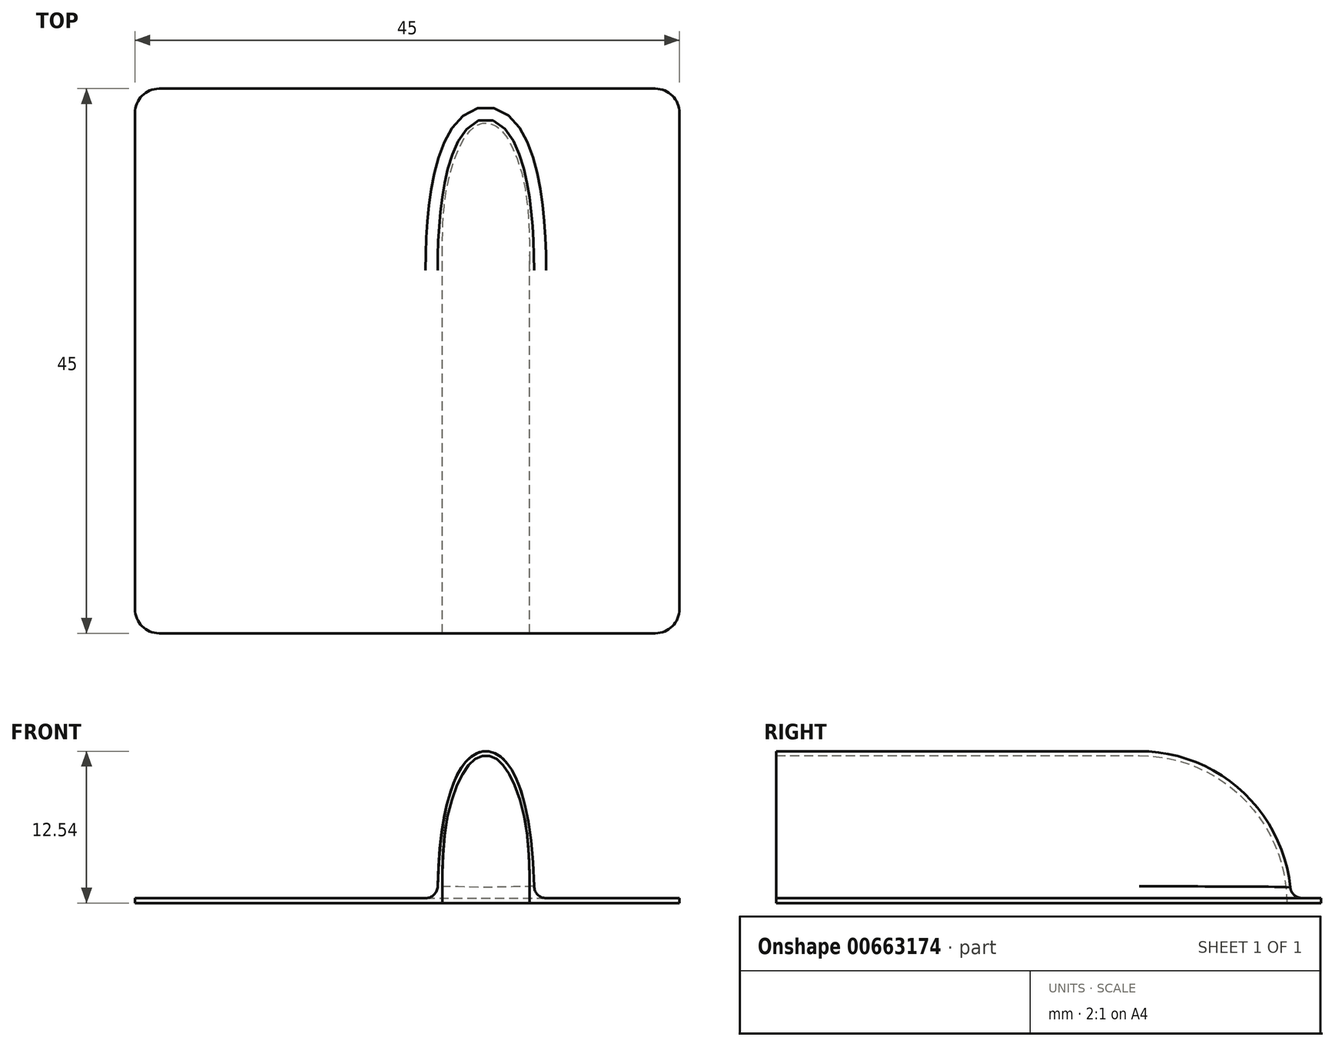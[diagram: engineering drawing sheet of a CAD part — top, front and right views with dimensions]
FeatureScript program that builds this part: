
annotation { "Feature Type Name" : "Feature", "Feature Type Description" : "" }
export const myFeature = defineFeature(function(context is Context, id is Id, definition is map)
    precondition{}
    {
        {
            var Q0;
            Q0=qCreatedBy(makeId("Top.planeOp"),FACE);
            var sketch = newSketch(context, id + "F0", { "sketchPlane" : qUnion([Q0])});
            skLineSegment(sketch, "E0.bottom", {"start": v(2, 45) * mm, "end": v(43, 45) * mm});
            skLineSegment(sketch, "E0.top", {"start": v(2, 0) * mm, "end": v(25, 0) * mm});
            skLineSegment(sketch, "E0.left", {"start": v(0, 43) * mm, "end": v(0, 2) * mm});
            skLineSegment(sketch, "E0.right", {"start": v(45, 43) * mm, "end": v(45, 2) * mm});
            skLineSegment(sketch, "E1.trimOffspring", {"start": v(33, 0) * mm, "end": v(43, 0) * mm});
            skLineSegment(sketch, "E2", {"start": v(25, 0) * mm, "end": v(25, 30) * mm});
            skLineSegment(sketch, "E3", {"start": v(33, 30) * mm, "end": v(33, 0) * mm});
            skPoint(sketch, "E4.visualSharp", {"position": v(0, 45) * mm});
            skArc(sketch, "E4.filletArc", {"start": v(2, 45) * mm, "mid": v(0.59, 44.41) * mm, "end": v(0, 43) * mm});
            skPoint(sketch, "E5.visualSharp", {"position": v(45, 45) * mm});
            skArc(sketch, "E5.filletArc", {"start": v(45, 43) * mm, "mid": v(44.41, 44.41) * mm, "end": v(43, 45) * mm});
            skPoint(sketch, "E6.visualSharp", {"position": v(45, 0) * mm});
            skArc(sketch, "E6.filletArc", {"start": v(43, 0) * mm, "mid": v(44.41, 0.59) * mm, "end": v(45, 2) * mm});
            skPoint(sketch, "E7.visualSharp", {"position": v(0, 0) * mm});
            skArc(sketch, "E7.filletArc", {"start": v(0, 2) * mm, "mid": v(0.59, 0.59) * mm, "end": v(2, 0) * mm});
            skFitSpline(sketch, "E8", {"points": [v(25, 30) * mm, v(29, 42.54) * mm, v(33, 30) * mm], "startDerivative": vector(0, 54.87) * mm, "endDerivative": vector(0, -54.87) * mm});
            skSolve(sketch);
        }
        {
            var Q0;
            Q0=qCreatedBy(makeId("Top.planeOp"),FACE);
            var sketch = newSketch(context, id + "F1", { "sketchPlane" : qUnion([Q0])});
            skFitSpline(sketch, "E9", {"points": [v(25, 30) * mm, v(29, 42.54) * mm, v(33, 30) * mm], "startDerivative": vector(0, 54.87) * mm, "endDerivative": vector(0, -54.87) * mm});
            skFitSpline(sketch, "E10.0", {"points": [v(25.4, 30) * mm, v(25.4, 32.27) * mm, v(25.65, 36.1) * mm, v(26.42, 39.23) * mm, v(27.2, 40.85) * mm, v(27.81, 41.64) * mm, v(28.42, 42.06) * mm, v(29, 42.18) * mm, v(29.58, 42.06) * mm, v(30.19, 41.64) * mm, v(30.8, 40.85) * mm, v(31.58, 39.23) * mm, v(32.35, 36.1) * mm, v(32.6, 32.27) * mm, v(32.6, 30) * mm]});
            skLineSegment(sketch, "E11", {"start": v(25, 30) * mm, "end": v(25.4, 30) * mm});
            skLineSegment(sketch, "E12", {"start": v(32.6, 30) * mm, "end": v(33, 30) * mm});
            skSolve(sketch);
        }
        {
            var Q0;
            Q0=qCreatedBy(makeId("Top.planeOp"),FACE);
            var sketch = newSketch(context, id + "F2", { "sketchPlane" : qUnion([Q0])});
            skLineSegment(sketch, "E13", {"start": v(20, 30) * mm, "end": v(28, 30) * mm});
            skSolve(sketch);
        }
        {
            var Q0;
            Q0=makeQuery(id+"F0.imprint","IMPRINT",FACE,{"disambiguationData":[TD([[makeQuery(id+"F0.imprint","IMPRINT",EDGE,{"derivedFrom":sQuery(id+"F0.wireOp",EDGE,"E0.bottom")}),-1.0]])]});
            extrude(context, id + "F3", {"entities" : qUnion([Q0]), "depth" : .4 * mm, "offsetDistance" : 25 * mm});
        }
        {
            var Q0;
            Q0=makeQuery(id+"F1.imprint","IMPRINT",FACE,{"disambiguationData":[TD([[makeQuery(id+"F1.imprint","IMPRINT",EDGE,{"derivedFrom":sQuery(id+"F1.wireOp",EDGE,"E9")}),-1.0]])]});
            var Q1;
            Q1=sQuery(id+"F2.wireOp",EDGE,"E13");
            revolve(context, id + "F4", {"operationType" : NewBodyOperationType.ADD, "entities" : qUnion([Q0]), "axis" : qUnion([Q1]), "revolveType" : RevolveType.ONE_DIRECTION, "angle" : 90 * degree});
        }
        {
            var Q0;
            Q0=makeQuery(id+"F4.opRevolve","CAP_FACE",FACE,{"disambiguationData":[OSD([sQuery(id+"F1.wireOp",EDGE,"E9"),sQuery(id+"F1.wireOp",EDGE,"E10.0"),sQuery(id+"F1.wireOp",EDGE,"E11"),sQuery(id+"F1.wireOp",EDGE,"E12")])],"isStart":false});
            var Q1;
            Q1 = qSketchRegion(id + "F2", true);
            extrude(context, id + "F5", {"entities" : qUnion([Q0, Q1]), "operationType" : NewBodyOperationType.ADD, "depth" : 30 * mm, "offsetDistance" : 25 * mm});
        }
        {
            var Q0;
            {var subQ0=sQuery(id+"F0.wireOp",EDGE,"E3");Q0=makeQuery(id+"F5.boolean.opBoolean","MERGE",EDGE,{"derivedFrom":[makeQuery(id+"F3.opExtrude","CAP_EDGE",EDGE,{"disambiguationData":[OSD([subQ0])],"isStart":false}),makeQuery(id+"F5.opExtrude","SWEPT_EDGE",EDGE,{"disambiguationData":[OSD([subQ0,sQuery(id+"F0.wireOp",EDGE,"E8")])]})]});}
            var Q1;
            {var subQ0=sQuery(id+"F1.wireOp",EDGE,"E9");Q1=makeQuery(id+"F5.boolean.opBoolean","MERGE",EDGE,{"derivedFrom":[makeQuery(id+"F4.boolean.opBoolean","SPLIT",EDGE,{"derivedFrom":makeQuery(id+"F4.opRevolve","CAP_EDGE",EDGE,{"disambiguationData":[OSD([subQ0])],"isStart":false})}),makeQuery(id+"F5.opExtrude","CAP_EDGE",EDGE,{"disambiguationData":[OSD([subQ0])],"isStart":true})]});}
            fillet(context, id + "F6", {"entities" : qUnion([Q0, Q1]), "radius" : 1 * mm, "tangentPropagation" : true, "allowEdgeOverflow" : false});
        }
    });
